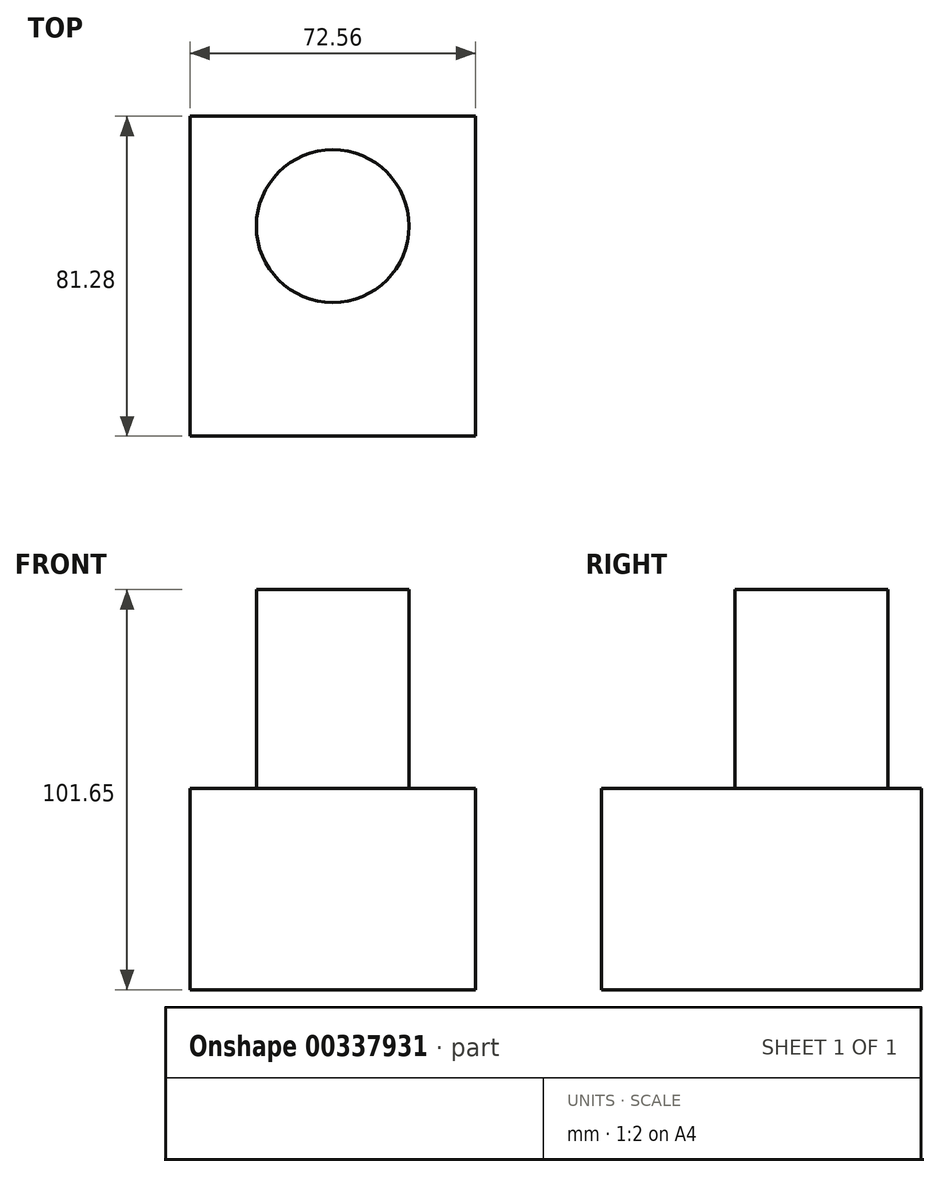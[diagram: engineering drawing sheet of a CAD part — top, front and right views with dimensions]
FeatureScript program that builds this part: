
annotation { "Feature Type Name" : "Feature", "Feature Type Description" : "" }
export const myFeature = defineFeature(function(context is Context, id is Id, definition is map)
    precondition{}
    {
        {
            var Q0;
            Q0=qCreatedBy(makeId("Front.planeOp"),FACE);
            var sketch = newSketch(context, id + "F0", { "sketchPlane" : qUnion([Q0])});
            skLineSegment(sketch, "E0.bottom", {"start": v(-36.28, -25.55) * mm, "end": v(36.28, -25.55) * mm});
            skLineSegment(sketch, "E0.top", {"start": v(-36.28, 25.55) * mm, "end": v(36.28, 25.55) * mm});
            skLineSegment(sketch, "E0.left", {"start": v(-36.28, -25.55) * mm, "end": v(-36.28, 25.55) * mm});
            skLineSegment(sketch, "E0.right", {"start": v(36.28, -25.55) * mm, "end": v(36.28, 25.55) * mm});
            skPoint(sketch, "E0.middle", {"position": v(0, 0) * mm});
            skSolve(sketch);
        }
        {
            var Q0;
            Q0 = qSketchRegion(id + "F0", true);
            extrude(context, id + "F1", {"entities" : qUnion([Q0]), "endBound" : BoundingType.SYMMETRIC, "depth" : 55.88 * mm});
        }
        {
            var Q0;
            Q0=makeQuery(id+"F1.opExtrude","SWEPT_FACE",FACE,{"disambiguationData":[OSD([sQuery(id+"F0.wireOp",EDGE,"E0.top")])]});
            var sketch = newSketch(context, id + "F2", { "sketchPlane" : qUnion([Q0])});
            skCircle(sketch, "E1", {"center": v(0, 0) * mm, "radius": 19.4 * mm});
            skSolve(sketch);
        }
        {
            var Q0;
            Q0 = qSketchRegion(id + "F2", true);
            extrude(context, id + "F3", {"entities" : qUnion([Q0]), "operationType" : NewBodyOperationType.ADD, "endBound" : BoundingType.SYMMETRIC, "depth" : 101.1 * mm});
        }
        {
            var Q0;
            Q0=makeQuery(id+"F1.opExtrude","CAP_FACE",FACE,{"disambiguationData":[OSD([sQuery(id+"F0.wireOp",EDGE,"E0.bottom"),sQuery(id+"F0.wireOp",EDGE,"E0.top"),sQuery(id+"F0.wireOp",EDGE,"E0.left"),sQuery(id+"F0.wireOp",EDGE,"E0.right")])],"isStart":false});
            extrude(context, id + "F4", {"entities" : qUnion([Q0]), "operationType" : NewBodyOperationType.ADD, "depth" : 25.4 * mm});
        }
    });
